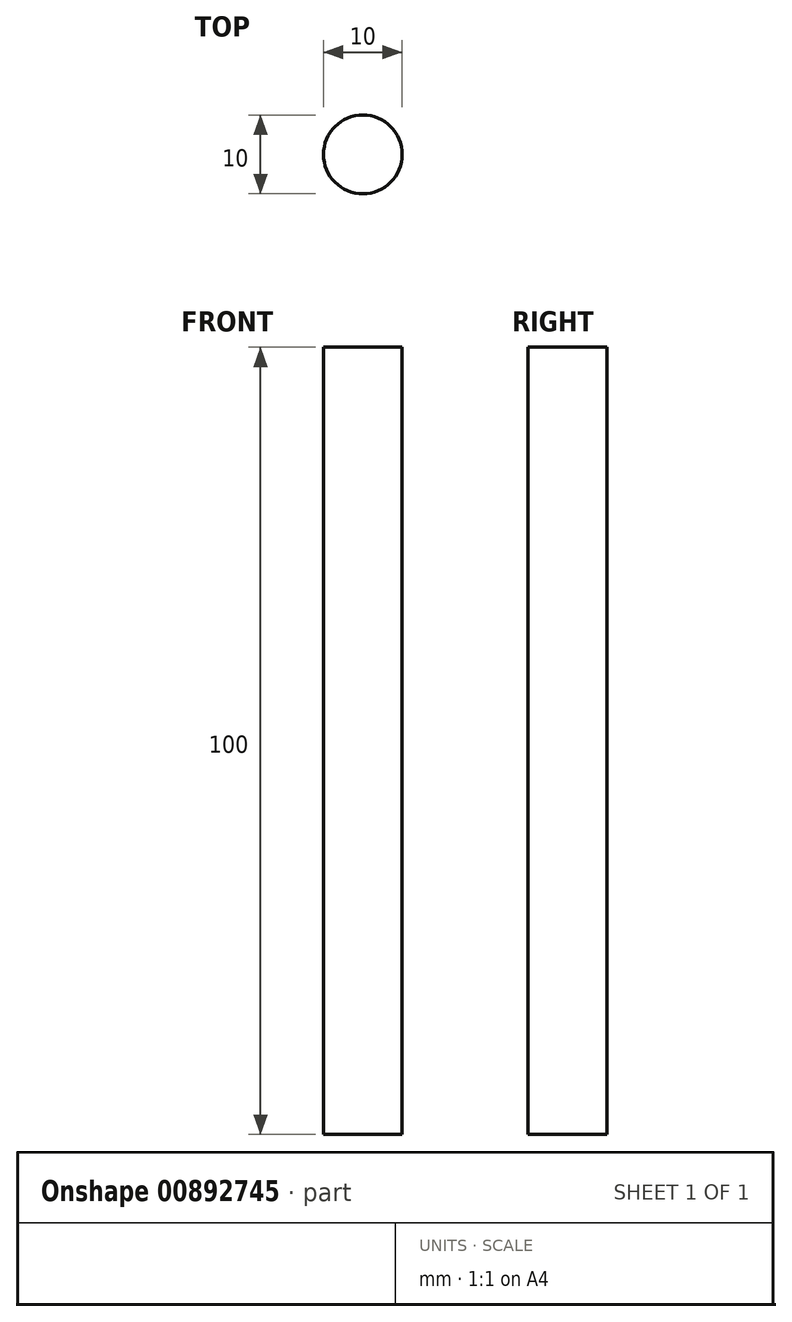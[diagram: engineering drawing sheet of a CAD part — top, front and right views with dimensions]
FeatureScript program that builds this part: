
annotation { "Feature Type Name" : "Feature", "Feature Type Description" : "" }
export const myFeature = defineFeature(function(context is Context, id is Id, definition is map)
    precondition{}
    {
        {
            var Q0;
            Q0=qCreatedBy(makeId("Top.planeOp"),FACE);
            var sketch = newSketch(context, id + "F0", { "sketchPlane" : qUnion([Q0])});
            skCircle(sketch, "E0", {"center": v(0, 0) * mm, "radius": 5 * mm});
            skSolve(sketch);
        }
        {
            var Q0;
            Q0=qSketchRegion(id+"F0",true);
            extrude(context, id + "F1", {"entities" : qUnion([Q0]), "depth" : 100 * mm, "offsetDistance" : 25 * mm});
        }
    });
